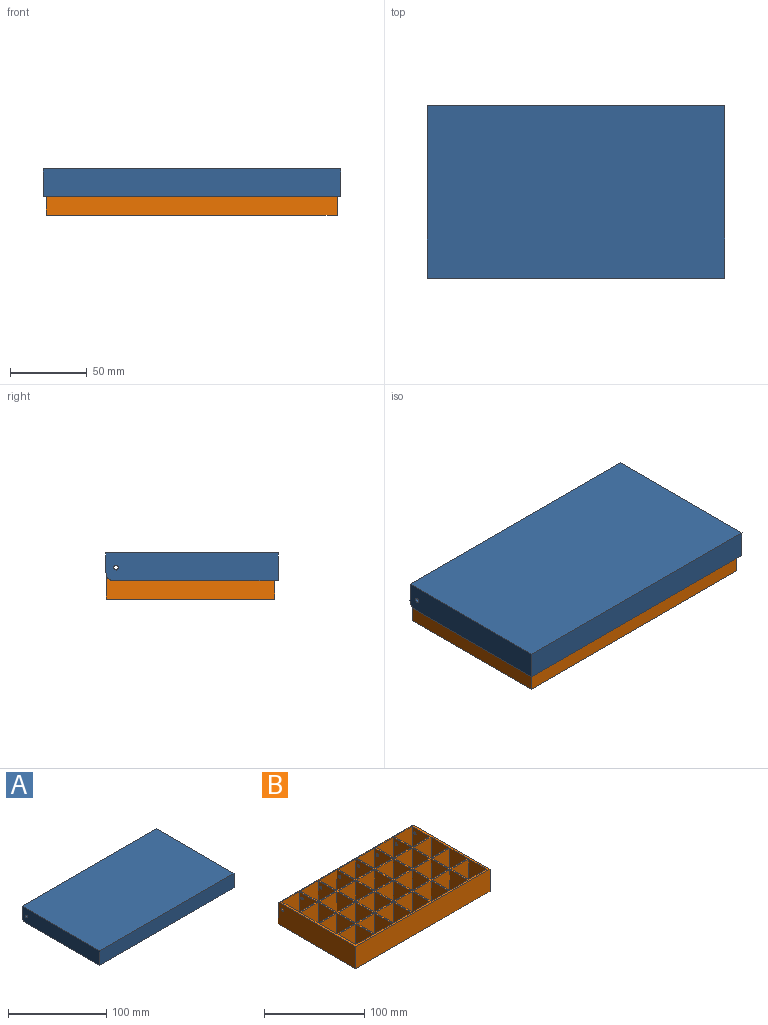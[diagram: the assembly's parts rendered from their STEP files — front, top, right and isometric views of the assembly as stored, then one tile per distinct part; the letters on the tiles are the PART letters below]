
ASSEMBLY  parts=2 mates=1
PART A: 14 faces, bbox 193.4x111.9x18 mm
  f0: plane 109.9x16mm, normal (1,0,0), area 1746mm2, adj f2,f6,f8,f9,f11,f13
  f1: plane 109.9x16mm, normal (-1,0,0), area 1746mm2, adj f2,f6,f8,f9,f10,f12
  f2: plane 189.4x16mm, normal (0,1,0), area 3030.4mm2, adj f0,f1,f8,f9
  f3: plane 111.9x18mm, normal (-1,0,0), area 2001.8mm2, adj f4,f6,f7,f8,f11,f13
  f4: plane 193.4x18mm, normal (0,-1,0), area 3481.2mm2, adj f3,f5,f7,f8
  f5: plane 111.9x18mm, normal (1,0,0), area 2001.8mm2, adj f4,f6,f7,f8,f10,f12
  f6: plane 193.4x13mm, normal (0,1,0), area 430.8mm2, adj f0,f1,f3,f5,f7,f9,f12,f13
  f7: plane 193.4x111.9mm, normal (0,0,1), area 21641.6mm2, adj f3,f4,f5,f6
  f8: plane 193.4x106.9mm, normal (0,0,-1), area 806.4mm2, adj f0,f1,f2,f3,f4,f5,f12,f13
  f9: plane 189.4x109.9mm, normal (0,0,-1), area 20815.2mm2, adj f0,f1,f2,f6
  f10: cylinder r=1.5mm len=3mm, axis (1,0,0), area 18.8mm2, adj f1,f5
  f11: cylinder r=1.5mm len=3mm, axis (1,0,0), area 18.8mm2, adj f0,f3
  f12: cylinder r=5mm len=5mm, axis (-1,0,0), area 15.7mm2, adj f1,f5,f6,f8
  f13: cylinder r=5mm len=5mm, axis (-1,0,0), area 15.7mm2, adj f0,f3,f6,f8
PART B: 183 faces, bbox 189x109.5x27 mm
  f0: plane 189x24mm, normal (0,1,0), area 4536mm2, adj f1,f115,f145,f174
  f1: plane 109.5x27mm, normal (-1,0,0), area 2947.5mm2, adj f0,f2,f116,f145,f174,f182
  f2: plane 189x27mm, normal (0,-1,0), area 5103.1mm2, adj f1,f115,f116,f145
  f3: plane 25x25mm, normal (0,-1,0), area 625mm2, adj f4,f87,f116,f144
  f4: plane 25x25mm, normal (-1,0,0), area 576.7mm2, adj f3,f5,f116,f144,f146
  f5: plane 25x10mm, normal (0,1,0), area 250mm2, adj f4,f87,f116,f146
  f6: plane 25x25mm, normal (0,-1,0), area 625mm2, adj f7,f88,f116,f143
  f7: plane 25x25mm, normal (-1,0,0), area 576.7mm2, adj f6,f8,f116,f143,f147
  f8: plane 25x10mm, normal (0,1,0), area 250mm2, adj f7,f88,f116,f147
  f9: plane 25x25mm, normal (0,-1,0), area 625mm2, adj f10,f89,f116,f142
  f10: plane 25x25mm, normal (-1,0,0), area 576.7mm2, adj f9,f11,f116,f142,f148
  f11: plane 25x10mm, normal (0,1,0), area 250mm2, adj f10,f89,f116,f148
  f12: plane 25x25mm, normal (0,-1,0), area 625mm2, adj f13,f90,f116,f141
  f13: plane 25x25mm, normal (-1,0,0), area 576.7mm2, adj f12,f14,f116,f141,f149
  f14: plane 25x10mm, normal (0,1,0), area 250mm2, adj f13,f90,f116,f149
  f15: plane 25x25mm, normal (0,-1,0), area 625mm2, adj f16,f91,f116,f140
  f16: plane 25x25mm, normal (-1,0,0), area 576.7mm2, adj f15,f17,f116,f140,f150
  f17: plane 25x10mm, normal (0,1,0), area 250mm2, adj f16,f91,f116,f150
  f18: plane 25x25mm, normal (0,-1,0), area 625mm2, adj f19,f92,f116,f139
  f19: plane 25x25mm, normal (-1,0,0), area 576.7mm2, adj f18,f20,f116,f139,f151
  f20: plane 25x10mm, normal (0,1,0), area 250mm2, adj f19,f92,f116,f151
  f21: plane 25x25mm, normal (-1,0,0), area 576.7mm2, adj f22,f93,f116,f138,f152
  f22: plane 25x10mm, normal (0,1,0), area 250mm2, adj f21,f23,f116,f152
  f23: plane 25x25mm, normal (1,0,0), area 576.7mm2, adj f22,f93,f116,f138,f152
  f24: plane 25x25mm, normal (0,-1,0), area 625mm2, adj f25,f94,f116,f137
  f25: plane 25x25mm, normal (-1,0,0), area 576.7mm2, adj f24,f26,f116,f137,f153
  f26: plane 25x10mm, normal (0,1,0), area 250mm2, adj f25,f94,f116,f153
  f27: plane 25x25mm, normal (0,-1,0), area 625mm2, adj f28,f95,f116,f136
  f28: plane 25x25mm, normal (-1,0,0), area 576.7mm2, adj f27,f29,f116,f136,f154
  f29: plane 25x10mm, normal (0,1,0), area 250mm2, adj f28,f95,f116,f154
  f30: plane 25x25mm, normal (0,-1,0), area 625mm2, adj f31,f96,f116,f135
  f31: plane 25x25mm, normal (-1,0,0), area 576.7mm2, adj f30,f32,f116,f135,f155
  f32: plane 25x10mm, normal (0,1,0), area 250mm2, adj f31,f96,f116,f155
  f33: plane 25x25mm, normal (0,-1,0), area 625mm2, adj f34,f97,f116,f134
  f34: plane 25x25mm, normal (-1,0,0), area 576.7mm2, adj f33,f35,f116,f134,f156
  f35: plane 25x10mm, normal (0,1,0), area 250mm2, adj f34,f97,f116,f156
  f36: plane 25x25mm, normal (0,-1,0), area 625mm2, adj f37,f98,f116,f133
  f37: plane 25x25mm, normal (-1,0,0), area 576.7mm2, adj f36,f38,f116,f133,f157
  f38: plane 25x10mm, normal (0,1,0), area 250mm2, adj f37,f98,f116,f157
  f39: plane 25x25mm, normal (0,-1,0), area 625mm2, adj f40,f99,f116,f132
  f40: plane 25x25mm, normal (-1,0,0), area 576.7mm2, adj f39,f41,f116,f132,f158
  f41: plane 25x10mm, normal (0,1,0), area 250mm2, adj f40,f99,f116,f158
  f42: plane 25x25mm, normal (-1,0,0), area 576.7mm2, adj f43,f100,f116,f131,f159
  f43: plane 25x10mm, normal (0,1,0), area 250mm2, adj f42,f44,f116,f159
  f44: plane 25x25mm, normal (1,0,0), area 576.7mm2, adj f43,f100,f116,f131,f159
  f45: plane 25x25mm, normal (0,-1,0), area 625mm2, adj f46,f101,f116,f130
  f46: plane 25x25mm, normal (-1,0,0), area 576.7mm2, adj f45,f47,f116,f130,f160
  f47: plane 25x10mm, normal (0,1,0), area 250mm2, adj f46,f101,f116,f160
  f48: plane 25x25mm, normal (0,-1,0), area 625mm2, adj f49,f102,f116,f129
  f49: plane 25x25mm, normal (-1,0,0), area 576.7mm2, adj f48,f50,f116,f129,f161
  f50: plane 25x10mm, normal (0,1,0), area 250mm2, adj f49,f102,f116,f161
  f51: plane 25x25mm, normal (0,-1,0), area 625mm2, adj f52,f103,f116,f128
  f52: plane 25x25mm, normal (-1,0,0), area 576.7mm2, adj f51,f53,f116,f128,f162
  f53: plane 25x10mm, normal (0,1,0), area 250mm2, adj f52,f103,f116,f162
  f54: plane 25x25mm, normal (0,-1,0), area 625mm2, adj f55,f104,f116,f127
  f55: plane 25x25mm, normal (-1,0,0), area 576.7mm2, adj f54,f56,f116,f127,f163
  f56: plane 25x10mm, normal (0,1,0), area 250mm2, adj f55,f104,f116,f163
  f57: plane 25x25mm, normal (0,-1,0), area 625mm2, adj f58,f105,f116,f126
  f58: plane 25x25mm, normal (-1,0,0), area 576.7mm2, adj f57,f59,f116,f126,f164
  f59: plane 25x10mm, normal (0,1,0), area 250mm2, adj f58,f105,f116,f164
  f60: plane 25x25mm, normal (0,-1,0), area 625mm2, adj f61,f106,f116,f125
  f61: plane 25x25mm, normal (-1,0,0), area 576.7mm2, adj f60,f62,f116,f125,f165
  f62: plane 25x10mm, normal (0,1,0), area 250mm2, adj f61,f106,f116,f165
  f63: plane 25x25mm, normal (-1,0,0), area 576.7mm2, adj f64,f107,f116,f124,f166
  f64: plane 25x10mm, normal (0,1,0), area 250mm2, adj f63,f65,f116,f166
  f65: plane 25x25mm, normal (1,0,0), area 576.7mm2, adj f64,f107,f116,f124,f166
  f66: plane 25x24.96mm, normal (0,-1,0), area 624mm2, adj f67,f108,f123,f174
  f67: plane 25x25mm, normal (-1,0,0), area 569.6mm2, adj f66,f68,f116,f123,f167,f174,f175
  f68: plane 25x10mm, normal (0,1,0), area 250mm2, adj f67,f108,f116,f167
  f69: plane 25x24.96mm, normal (0,-1,0), area 624mm2, adj f70,f109,f122,f174
  f70: plane 25x25mm, normal (-1,0,0), area 569.6mm2, adj f69,f71,f116,f122,f168,f174,f181
  f71: plane 25x10mm, normal (0,1,0), area 250mm2, adj f70,f109,f116,f168
  f72: plane 25x24.96mm, normal (0,-1,0), area 624mm2, adj f73,f110,f121,f174
  f73: plane 25x25mm, normal (-1,0,0), area 569.6mm2, adj f72,f74,f116,f121,f169,f174,f180
  f74: plane 25x10mm, normal (0,1,0), area 250mm2, adj f73,f110,f116,f169
  f75: plane 25x24.96mm, normal (0,-1,0), area 624mm2, adj f76,f111,f120,f174
  f76: plane 25x25mm, normal (-1,0,0), area 569.6mm2, adj f75,f77,f116,f120,f170,f174,f179
  f77: plane 25x10mm, normal (0,1,0), area 250mm2, adj f76,f111,f116,f170
  f78: plane 25x24.96mm, normal (0,-1,0), area 624mm2, adj f79,f112,f119,f174
  f79: plane 25x25mm, normal (-1,0,0), area 569.6mm2, adj f78,f80,f116,f119,f171,f174,f178
  f80: plane 25x10mm, normal (0,1,0), area 250mm2, adj f79,f112,f116,f171
  f81: plane 25x24.96mm, normal (0,-1,0), area 624mm2, adj f82,f113,f118,f174
  f82: plane 25x25mm, normal (-1,0,0), area 569.6mm2, adj f81,f83,f116,f118,f172,f174,f177
  f83: plane 25x10mm, normal (0,1,0), area 250mm2, adj f82,f113,f116,f172
  f84: plane 25x25mm, normal (-1,0,0), area 569.6mm2, adj f85,f114,f116,f117,f173,f174,f176
  f85: plane 25x10mm, normal (0,1,0), area 250mm2, adj f84,f86,f116,f173
  f86: plane 25x25mm, normal (1,0,0), area 569.6mm2, adj f85,f114,f116,f117,f173,f174,f182
  f87: plane 25x25mm, normal (1,0,0), area 576.7mm2, adj f3,f5,f116,f144,f146
  f88: plane 25x25mm, normal (1,0,0), area 576.7mm2, adj f6,f8,f116,f143,f147
  f89: plane 25x25mm, normal (1,0,0), area 576.7mm2, adj f9,f11,f116,f142,f148
  f90: plane 25x25mm, normal (1,0,0), area 576.7mm2, adj f12,f14,f116,f141,f149
  f91: plane 25x25mm, normal (1,0,0), area 576.7mm2, adj f15,f17,f116,f140,f150
  f92: plane 25x25mm, normal (1,0,0), area 576.7mm2, adj f18,f20,f116,f139,f151
  f93: plane 25x25mm, normal (0,-1,0), area 625mm2, adj f21,f23,f116,f138
  f94: plane 25x25mm, normal (1,0,0), area 576.7mm2, adj f24,f26,f116,f137,f153
  f95: plane 25x25mm, normal (1,0,0), area 576.7mm2, adj f27,f29,f116,f136,f154
  f96: plane 25x25mm, normal (1,0,0), area 576.7mm2, adj f30,f32,f116,f135,f155
  f97: plane 25x25mm, normal (1,0,0), area 576.7mm2, adj f33,f35,f116,f134,f156
  f98: plane 25x25mm, normal (1,0,0), area 576.7mm2, adj f36,f38,f116,f133,f157
  f99: plane 25x25mm, normal (1,0,0), area 576.7mm2, adj f39,f41,f116,f132,f158
  f100: plane 25x25mm, normal (0,-1,0), area 625mm2, adj f42,f44,f116,f131
  f101: plane 25x25mm, normal (1,0,0), area 576.7mm2, adj f45,f47,f116,f130,f160
  f102: plane 25x25mm, normal (1,0,0), area 576.7mm2, adj f48,f50,f116,f129,f161
  f103: plane 25x25mm, normal (1,0,0), area 576.7mm2, adj f51,f53,f116,f128,f162
  f104: plane 25x25mm, normal (1,0,0), area 576.7mm2, adj f54,f56,f116,f127,f163
  f105: plane 25x25mm, normal (1,0,0), area 576.7mm2, adj f57,f59,f116,f126,f164
  f106: plane 25x25mm, normal (1,0,0), area 576.7mm2, adj f60,f62,f116,f125,f165
  f107: plane 25x25mm, normal (0,-1,0), area 625mm2, adj f63,f65,f116,f124
  f108: plane 25x25mm, normal (1,0,0), area 569.6mm2, adj f66,f68,f116,f123,f167,f174,f181
  f109: plane 25x25mm, normal (1,0,0), area 569.6mm2, adj f69,f71,f116,f122,f168,f174,f180
  f110: plane 25x25mm, normal (1,0,0), area 569.6mm2, adj f72,f74,f116,f121,f169,f174,f179
  f111: plane 25x25mm, normal (1,0,0), area 569.6mm2, adj f75,f77,f116,f120,f170,f174,f178
  f112: plane 25x25mm, normal (1,0,0), area 569.6mm2, adj f78,f80,f116,f119,f171,f174,f177
  f113: plane 25x25mm, normal (1,0,0), area 569.6mm2, adj f81,f83,f116,f118,f172,f174,f176
  f114: plane 25x24.96mm, normal (0,-1,0), area 624mm2, adj f84,f86,f117,f174
  f115: plane 109.5x27mm, normal (1,0,0), area 2947.5mm2, adj f0,f2,f116,f145,f174,f175
  f116: plane 189x106.5mm, normal (0,0,1), area 2716.2mm2, adj f1,f2,f3,f4,f5,f6,f7,f8
  f117: plane 25x10mm, normal (0,0,1), area 250mm2, adj f84,f86,f114,f173
  f118: plane 25x10mm, normal (0,0,1), area 250mm2, adj f81,f82,f113,f172
  f119: plane 25x10mm, normal (0,0,1), area 250mm2, adj f78,f79,f112,f171
  f120: plane 25x10mm, normal (0,0,1), area 250mm2, adj f75,f76,f111,f170
  f121: plane 25x10mm, normal (0,0,1), area 250mm2, adj f72,f73,f110,f169
  f122: plane 25x10mm, normal (0,0,1), area 250mm2, adj f69,f70,f109,f168
  f123: plane 25x10mm, normal (0,0,1), area 250mm2, adj f66,f67,f108,f167
  f124: plane 25x10mm, normal (0,0,1), area 250mm2, adj f63,f65,f107,f166
  f125: plane 25x10mm, normal (0,0,1), area 250mm2, adj f60,f61,f106,f165
  f126: plane 25x10mm, normal (0,0,1), area 250mm2, adj f57,f58,f105,f164
  f127: plane 25x10mm, normal (0,0,1), area 250mm2, adj f54,f55,f104,f163
  f128: plane 25x10mm, normal (0,0,1), area 250mm2, adj f51,f52,f103,f162
  f129: plane 25x10mm, normal (0,0,1), area 250mm2, adj f48,f49,f102,f161
  f130: plane 25x10mm, normal (0,0,1), area 250mm2, adj f45,f46,f101,f160
  f131: plane 25x10mm, normal (0,0,1), area 250mm2, adj f42,f44,f100,f159
  f132: plane 25x10mm, normal (0,0,1), area 250mm2, adj f39,f40,f99,f158
  f133: plane 25x10mm, normal (0,0,1), area 250mm2, adj f36,f37,f98,f157
  f134: plane 25x10mm, normal (0,0,1), area 250mm2, adj f33,f34,f97,f156
  f135: plane 25x10mm, normal (0,0,1), area 250mm2, adj f30,f31,f96,f155
  f136: plane 25x10mm, normal (0,0,1), area 250mm2, adj f27,f28,f95,f154
  f137: plane 25x10mm, normal (0,0,1), area 250mm2, adj f24,f25,f94,f153
  f138: plane 25x10mm, normal (0,0,1), area 250mm2, adj f21,f23,f93,f152
  f139: plane 25x10mm, normal (0,0,1), area 250mm2, adj f18,f19,f92,f151
  f140: plane 25x10mm, normal (0,0,1), area 250mm2, adj f15,f16,f91,f150
  f141: plane 25x10mm, normal (0,0,1), area 250mm2, adj f12,f13,f90,f149
  f142: plane 25x10mm, normal (0,0,1), area 250mm2, adj f9,f10,f89,f148
  f143: plane 25x10mm, normal (0,0,1), area 250mm2, adj f6,f7,f88,f147
  f144: plane 25x10mm, normal (0,0,1), area 250mm2, adj f3,f4,f87,f146
  f145: plane 189x109.5mm, normal (0,0,-1), area 20695.7mm2, adj f0,f1,f2,f115
  f146: cylinder r=15mm len=25mm, axis (-1,0,0), area 589mm2, adj f4,f5,f87,f144
  f147: cylinder r=15mm len=25mm, axis (-1,0,0), area 589mm2, adj f7,f8,f88,f143
  f148: cylinder r=15mm len=25mm, axis (-1,0,0), area 589mm2, adj f10,f11,f89,f142
  f149: cylinder r=15mm len=25mm, axis (-1,0,0), area 589mm2, adj f13,f14,f90,f141
  f150: cylinder r=15mm len=25mm, axis (-1,0,0), area 589mm2, adj f16,f17,f91,f140
  f151: cylinder r=15mm len=25mm, axis (-1,0,0), area 589mm2, adj f19,f20,f92,f139
  f152: cylinder r=15mm len=25mm, axis (-1,0,0), area 589mm2, adj f21,f22,f23,f138
  f153: cylinder r=15mm len=25mm, axis (-1,0,0), area 589mm2, adj f25,f26,f94,f137
  f154: cylinder r=15mm len=25mm, axis (-1,0,0), area 589mm2, adj f28,f29,f95,f136
  f155: cylinder r=15mm len=25mm, axis (-1,0,0), area 589mm2, adj f31,f32,f96,f135
  f156: cylinder r=15mm len=25mm, axis (-1,0,0), area 589mm2, adj f34,f35,f97,f134
  f157: cylinder r=15mm len=25mm, axis (-1,0,0), area 589mm2, adj f37,f38,f98,f133
  f158: cylinder r=15mm len=25mm, axis (-1,0,0), area 589mm2, adj f40,f41,f99,f132
  f159: cylinder r=15mm len=25mm, axis (-1,0,0), area 589mm2, adj f42,f43,f44,f131
  f160: cylinder r=15mm len=25mm, axis (-1,0,0), area 589mm2, adj f46,f47,f101,f130
  f161: cylinder r=15mm len=25mm, axis (-1,0,0), area 589mm2, adj f49,f50,f102,f129
  f162: cylinder r=15mm len=25mm, axis (-1,0,0), area 589mm2, adj f52,f53,f103,f128
  f163: cylinder r=15mm len=25mm, axis (-1,0,0), area 589mm2, adj f55,f56,f104,f127
  f164: cylinder r=15mm len=25mm, axis (-1,0,0), area 589mm2, adj f58,f59,f105,f126
  f165: cylinder r=15mm len=25mm, axis (-1,0,0), area 589mm2, adj f61,f62,f106,f125
  f166: cylinder r=15mm len=25mm, axis (-1,0,0), area 589mm2, adj f63,f64,f65,f124
  f167: cylinder r=15mm len=25mm, axis (-1,0,0), area 589mm2, adj f67,f68,f108,f123
  f168: cylinder r=15mm len=25mm, axis (-1,0,0), area 589mm2, adj f70,f71,f109,f122
  f169: cylinder r=15mm len=25mm, axis (-1,0,0), area 589mm2, adj f73,f74,f110,f121
  f170: cylinder r=15mm len=25mm, axis (-1,0,0), area 589mm2, adj f76,f77,f111,f120
  f171: cylinder r=15mm len=25mm, axis (-1,0,0), area 589mm2, adj f79,f80,f112,f119
  f172: cylinder r=15mm len=25mm, axis (-1,0,0), area 589mm2, adj f82,f83,f113,f118
  f173: cylinder r=15mm len=25mm, axis (-1,0,0), area 589mm2, adj f84,f85,f86,f117
  f174: cylinder r=3mm len=189mm, axis (1,0,0), area 802.7mm2, adj f0,f1,f66,f67,f69,f70,f72,f73
  f175: cylinder r=1.5mm len=3mm, axis (1,0,0), area 23.6mm2, adj f67,f115
  f176: cylinder r=1.5mm len=3mm, axis (1,0,0), area 14.1mm2, adj f84,f113
  f177: cylinder r=1.5mm len=3mm, axis (1,0,0), area 14.1mm2, adj f82,f112
  f178: cylinder r=1.5mm len=3mm, axis (1,0,0), area 14.1mm2, adj f79,f111
  f179: cylinder r=1.5mm len=3mm, axis (1,0,0), area 14.1mm2, adj f76,f110
  f180: cylinder r=1.5mm len=3mm, axis (1,0,0), area 14.1mm2, adj f73,f109
  f181: cylinder r=1.5mm len=3mm, axis (1,0,0), area 14.1mm2, adj f70,f108
  f182: cylinder r=1.5mm len=3mm, axis (1,0,0), area 23.6mm2, adj f1,f86
PLACE A rot(axis=(0.01,0,-1),0deg) t=(-2.28,50.33,15.08)mm
PLACE B rot(axis=(0,0,-1),0deg) t=(-2.48,50.33,15.08)mm
MATE pin_slot A.f10 <-> B.f175  axis (1,0,0) through (-17.48,58.99,33.48)mm
